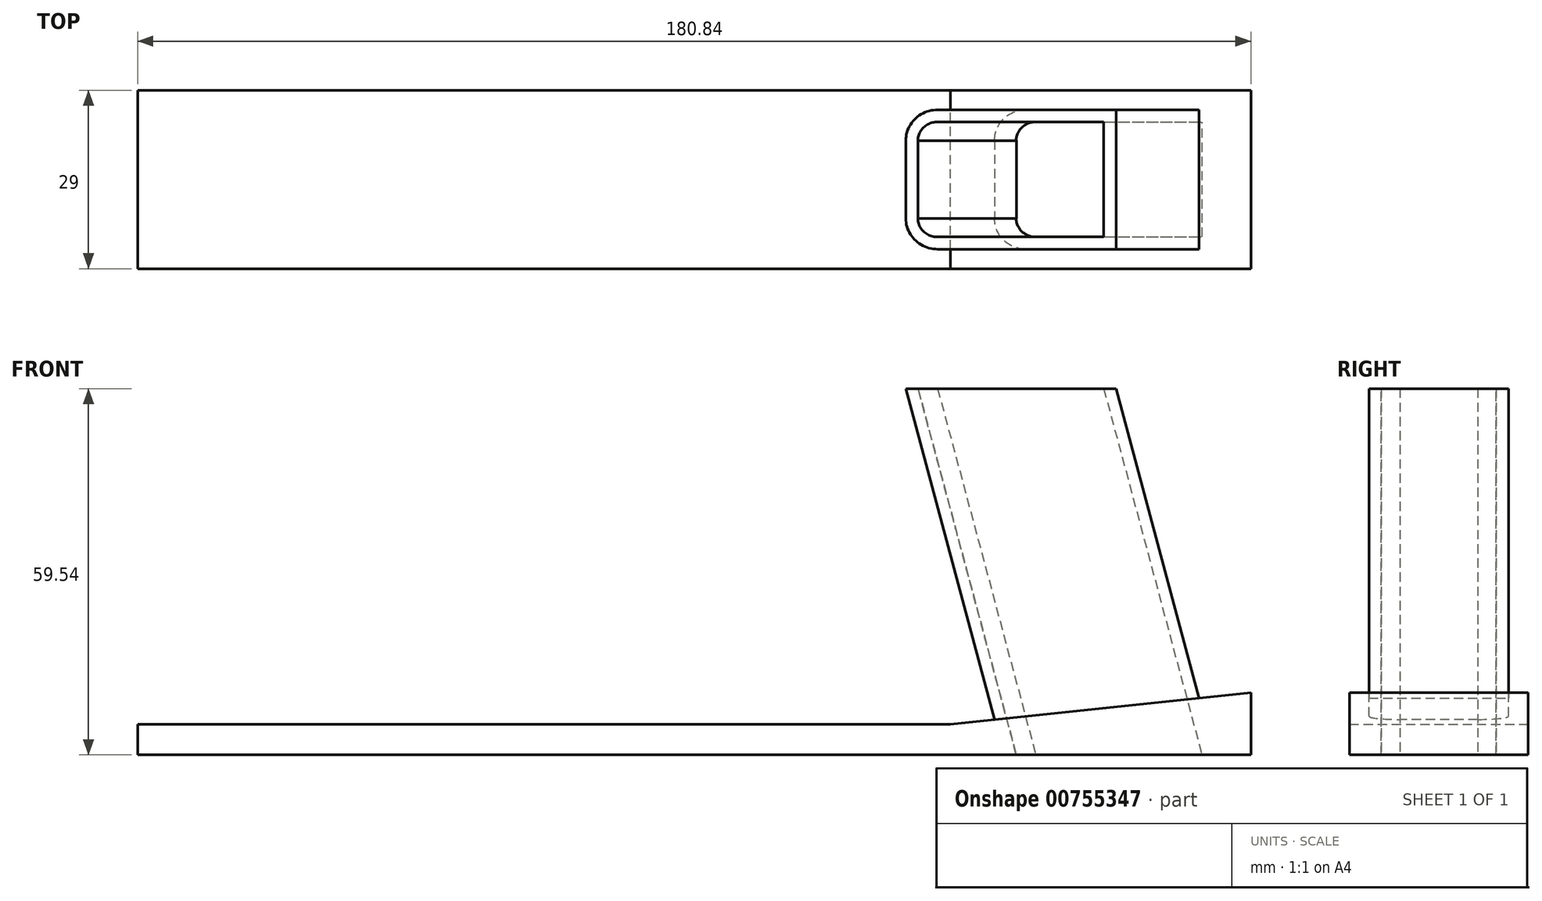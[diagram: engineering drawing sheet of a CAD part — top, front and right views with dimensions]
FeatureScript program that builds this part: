
annotation { "Feature Type Name" : "Feature", "Feature Type Description" : "" }
export const myFeature = defineFeature(function(context is Context, id is Id, definition is map)
    precondition{}
    {
        {
            var Q0;
            Q0=qCreatedBy(makeId("Front.planeOp"),FACE);
            var sketch = newSketch(context, id + "F0", { "sketchPlane" : qUnion([Q0])});
            skLineSegment(sketch, "E0", {"start": v(-17.08, 0) * mm, "end": v(17.08, 0) * mm, "construction": true});
            skLineSegment(sketch, "E1", {"start": v(17.08, 0) * mm, "end": v(1.13, 59.54) * mm, "construction": true});
            skLineSegment(sketch, "E2", {"start": v(-33.04, 59.54) * mm, "end": v(-17.08, 0) * mm, "construction": true});
            skLineSegment(sketch, "E3", {"start": v(1.77, 59.54) * mm, "end": v(17.73, 0) * mm, "construction": true});
            skLineSegment(sketch, "E4", {"start": v(-17.73, 0) * mm, "end": v(-33.68, 59.54) * mm, "construction": true});
            skLineSegment(sketch, "E5", {"start": v(-33.68, 59.54) * mm, "end": v(1.77, 59.54) * mm, "construction": true});
            skLineSegment(sketch, "E6", {"start": v(0, 0) * mm, "end": v(-15.95, 59.54) * mm, "construction": true});
            skLineSegment(sketch, "E7", {"start": v(-75, 0) * mm, "end": v(75, 0) * mm, "construction": true});
            skLineSegment(sketch, "E8", {"start": v(-24.46, 0) * mm, "end": v(-25.8, 5) * mm, "construction": true});
            skLineSegment(sketch, "E9", {"start": v(-24.46, 0) * mm, "end": v(25.75, 0) * mm, "construction": true});
            skLineSegment(sketch, "E10", {"start": v(25.75, 0) * mm, "end": v(23.04, 10.13) * mm, "construction": true});
            skLineSegment(sketch, "E11", {"start": v(23.04, 10.13) * mm, "end": v(-25.8, 5) * mm, "construction": true});
            skLineSegment(sketch, "E12", {"start": v(-25.8, 5) * mm, "end": v(24.41, 5) * mm, "construction": true});
            skLineSegment(sketch, "E13", {"start": v(-17.08, 0) * mm, "end": v(-33.04, 59.54) * mm});
            skLineSegment(sketch, "E14", {"start": v(-33.04, 59.54) * mm, "end": v(0.2, 63.03) * mm, "construction": true});
            skLineSegment(sketch, "E15", {"start": v(17.08, 0) * mm, "end": v(-17.08, 0) * mm});
            skLineSegment(sketch, "E16", {"start": v(-33.04, 59.54) * mm, "end": v(1.13, 59.54) * mm});
            skLineSegment(sketch, "E17", {"start": v(1.13, 59.54) * mm, "end": v(17.08, 0) * mm});
            skSolve(sketch);
        }
        {
            var Q0;
            Q0 = qSketchRegion(id + "F0", true);
            extrude(context, id + "F1", {"entities" : qUnion([Q0]), "endBound" : BoundingType.SYMMETRIC, "depth" : 22.65 * mm, "offsetDistance" : 25 * mm});
        }
        {
            var Q0;
            Q0=qCreatedBy(makeId("Front.planeOp"),FACE);
            var sketch = newSketch(context, id + "F2", { "sketchPlane" : qUnion([Q0])});
            skLineSegment(sketch, "E18", {"start": v(-25.8, 5) * mm, "end": v(-24.46, 0) * mm, "construction": true});
            skLineSegment(sketch, "E19", {"start": v(23.04, 10.13) * mm, "end": v(-25.8, 5) * mm});
            skLineSegment(sketch, "E20", {"start": v(-25.8, 5) * mm, "end": v(-25.8, 0) * mm});
            skLineSegment(sketch, "E21", {"start": v(-25.8, 0) * mm, "end": v(23.04, 0) * mm});
            skLineSegment(sketch, "E22", {"start": v(23.04, 0) * mm, "end": v(23.04, 10.13) * mm});
            skLineSegment(sketch, "E23", {"start": v(-25.8, 0) * mm, "end": v(25.75, 0) * mm, "construction": true});
            skLineSegment(sketch, "E24", {"start": v(25.75, 0) * mm, "end": v(23.04, 10.13) * mm, "construction": true});
            skSolve(sketch);
        }
        {
            var Q0;
            Q0 = qSketchRegion(id + "F2", true);
            extrude(context, id + "F3", {"entities" : qUnion([Q0]), "operationType" : NewBodyOperationType.ADD, "endBound" : BoundingType.SYMMETRIC, "depth" : 29 * mm, "offsetDistance" : 25 * mm});
        }
        {
            var Q0;
            Q0=makeQuery(id+"F1.opExtrude","CAP_EDGE",EDGE,{"disambiguationData":[OSD([sQuery(id+"F0.wireOp",EDGE,"E13")])],"isStart":true});
            var Q1;
            Q1=makeQuery(id+"F1.opExtrude","CAP_EDGE",EDGE,{"disambiguationData":[OSD([sQuery(id+"F0.wireOp",EDGE,"E13")])],"isStart":false});
            fillet(context, id + "F4", {"entities" : qUnion([Q0, Q1]), "radius" : 5 * mm, "tangentPropagation" : true, "allowEdgeOverflow" : false});
        }
        {
            var Q0;
            Q0=qCreatedBy(makeId("Front.planeOp"),FACE);
            var sketch = newSketch(context, id + "F5", { "sketchPlane" : qUnion([Q0])});
            skLineSegment(sketch, "E25", {"start": v(0, 0) * mm, "end": v(-15.95, 59.54) * mm});
            skSolve(sketch);
        }
        {
            var Q0;
            Q0=makeQuery(id+"F1.opExtrude","SWEPT_FACE",FACE,{"disambiguationData":[OSD([sQuery(id+"F0.wireOp",EDGE,"E16")])]});
            var sketch = newSketch(context, id + "F6", { "sketchPlane" : qUnion([Q0])});
            skLineSegment(sketch, "E26.0", {"start": v(-27.86, 9.32) * mm, "end": v(-0.87, 9.32) * mm});
            skLineSegment(sketch, "E26.1", {"start": v(-31.04, -6.33) * mm, "end": v(-31.04, 6.32) * mm});
            skFitSpline(sketch, "E26.2", {"points": [v(-31.04, -6.33) * mm, v(-31.04, -6.71) * mm, v(-30.92, -7.28) * mm, v(-30.54, -7.97) * mm, v(-30.15, -8.44) * mm, v(-29.66, -8.82) * mm, v(-28.92, -9.2) * mm, v(-28.3, -9.32) * mm, v(-27.86, -9.32) * mm]});
            skFitSpline(sketch, "E26.3", {"points": [v(-27.86, 9.32) * mm, v(-28.3, 9.32) * mm, v(-28.92, 9.2) * mm, v(-29.66, 8.82) * mm, v(-30.15, 8.44) * mm, v(-30.54, 7.97) * mm, v(-30.92, 7.28) * mm, v(-31.04, 6.71) * mm, v(-31.04, 6.33) * mm]});
            skLineSegment(sketch, "E26.4", {"start": v(-27.86, -9.32) * mm, "end": v(-0.87, -9.32) * mm});
            skLineSegment(sketch, "E26.5", {"start": v(-0.87, -9.32) * mm, "end": v(-0.87, 9.32) * mm});
            skSolve(sketch);
        }
        {
            var Q0;
            Q0=makeQuery(id+"F6.imprint","IMPRINT",FACE,{"disambiguationData":[TD([[makeQuery(id+"F6.imprint","IMPRINT",EDGE,{"derivedFrom":sQuery(id+"F6.wireOp",EDGE,"E26.0")}),-1.0]])]});
            var Q1;
            Q1=sQuery(id+"F5.wireOp",EDGE,"E25");
            sweep(context, id + "F7", {"operationType" : NewBodyOperationType.REMOVE, "profiles" : qUnion([Q0]), "path" : qUnion([Q1])});
        }
        {
            var Q0;
            Q0=makeQuery(id+"F3.opExtrude","SWEPT_FACE",FACE,{"disambiguationData":[OSD([sQuery(id+"F2.wireOp",EDGE,"E20")])]});
            var sketch = newSketch(context, id + "F8", { "sketchPlane" : qUnion([Q0])});
            skLineSegment(sketch, "E27.bottom", {"start": v(-14.5, 5) * mm, "end": v(14.5, 5) * mm});
            skLineSegment(sketch, "E27.top", {"start": v(-14.5, 0) * mm, "end": v(14.5, 0) * mm});
            skLineSegment(sketch, "E27.left", {"start": v(-14.5, 5) * mm, "end": v(-14.5, 0) * mm});
            skLineSegment(sketch, "E27.right", {"start": v(14.5, 5) * mm, "end": v(14.5, 0) * mm});
            skSolve(sketch);
        }
        {
            var Q0;
            Q0 = qSketchRegion(id + "F8", true);
            extrude(context, id + "F9", {"entities" : qUnion([Q0]), "operationType" : NewBodyOperationType.ADD, "depth" : 132 * mm, "offsetDistance" : 25 * mm});
        }
    });
